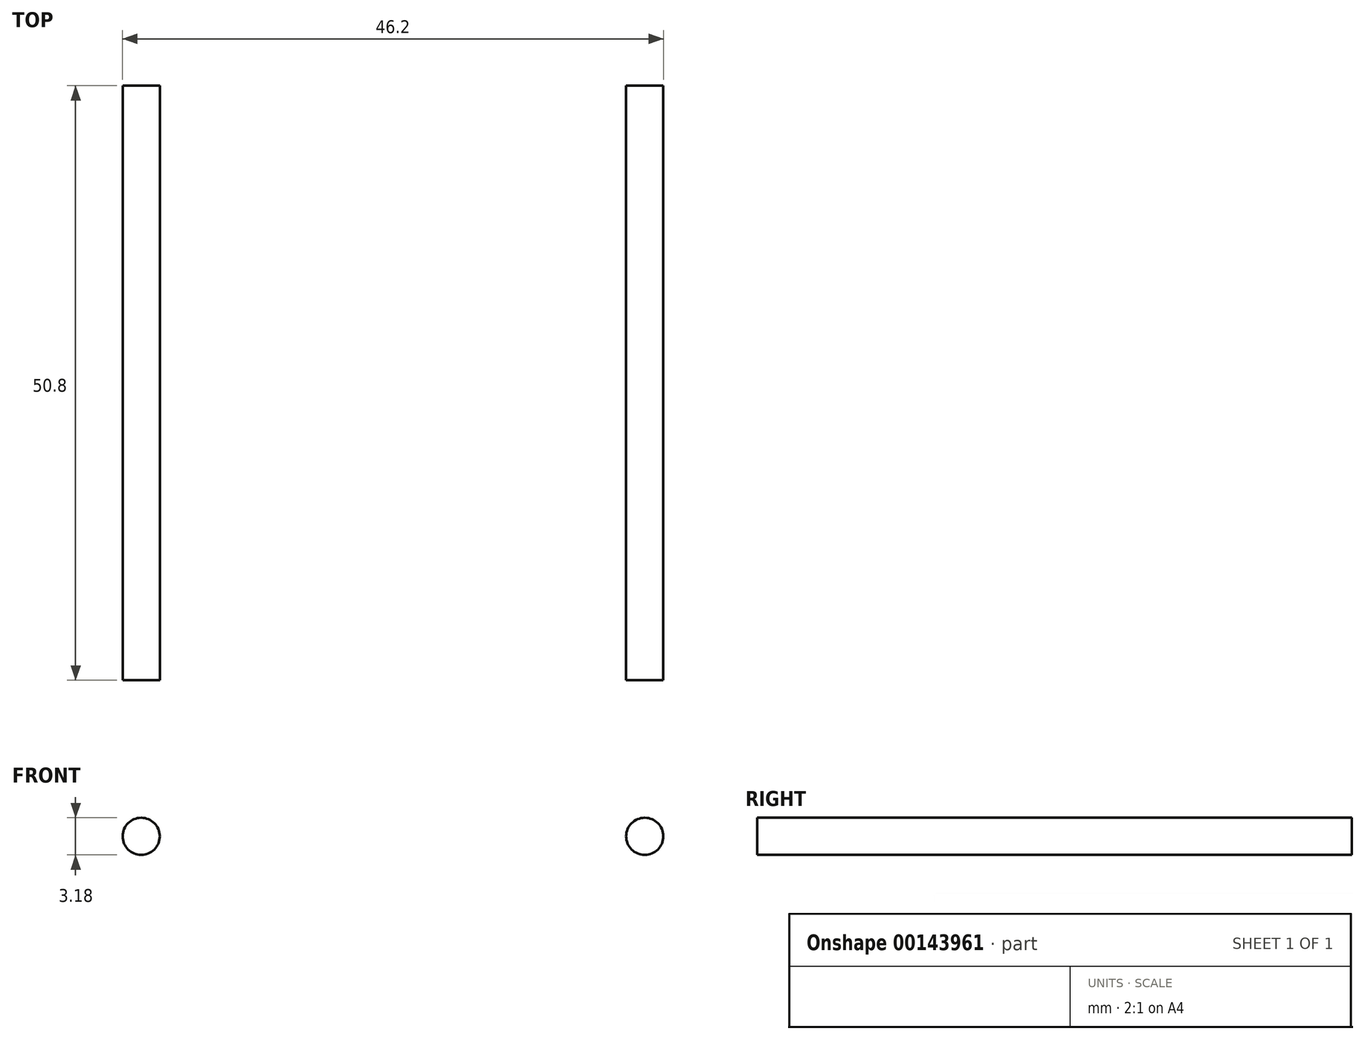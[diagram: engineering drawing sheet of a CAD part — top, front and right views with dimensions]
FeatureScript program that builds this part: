
annotation { "Feature Type Name" : "Feature", "Feature Type Description" : "" }
export const myFeature = defineFeature(function(context is Context, id is Id, definition is map)
    precondition{}
    {
        {
            var Q0;
            Q0=qCreatedBy(makeId("Front.planeOp"),FACE);
            var sketch = newSketch(context, id + "F0", { "sketchPlane" : qUnion([Q0])});
            skCircle(sketch, "E0", {"center": v(-24.17, 0) * mm, "radius": 1.59 * mm});
            skCircle(sketch, "E1", {"center": v(18.85, 0) * mm, "radius": 1.59 * mm});
            skSolve(sketch);
        }
        {
            var Q0;
            Q0 = qSketchRegion(id + "F0", true);
            extrude(context, id + "F1", {"entities" : qUnion([Q0]), "depth" : 50.8 * mm});
        }
    });
